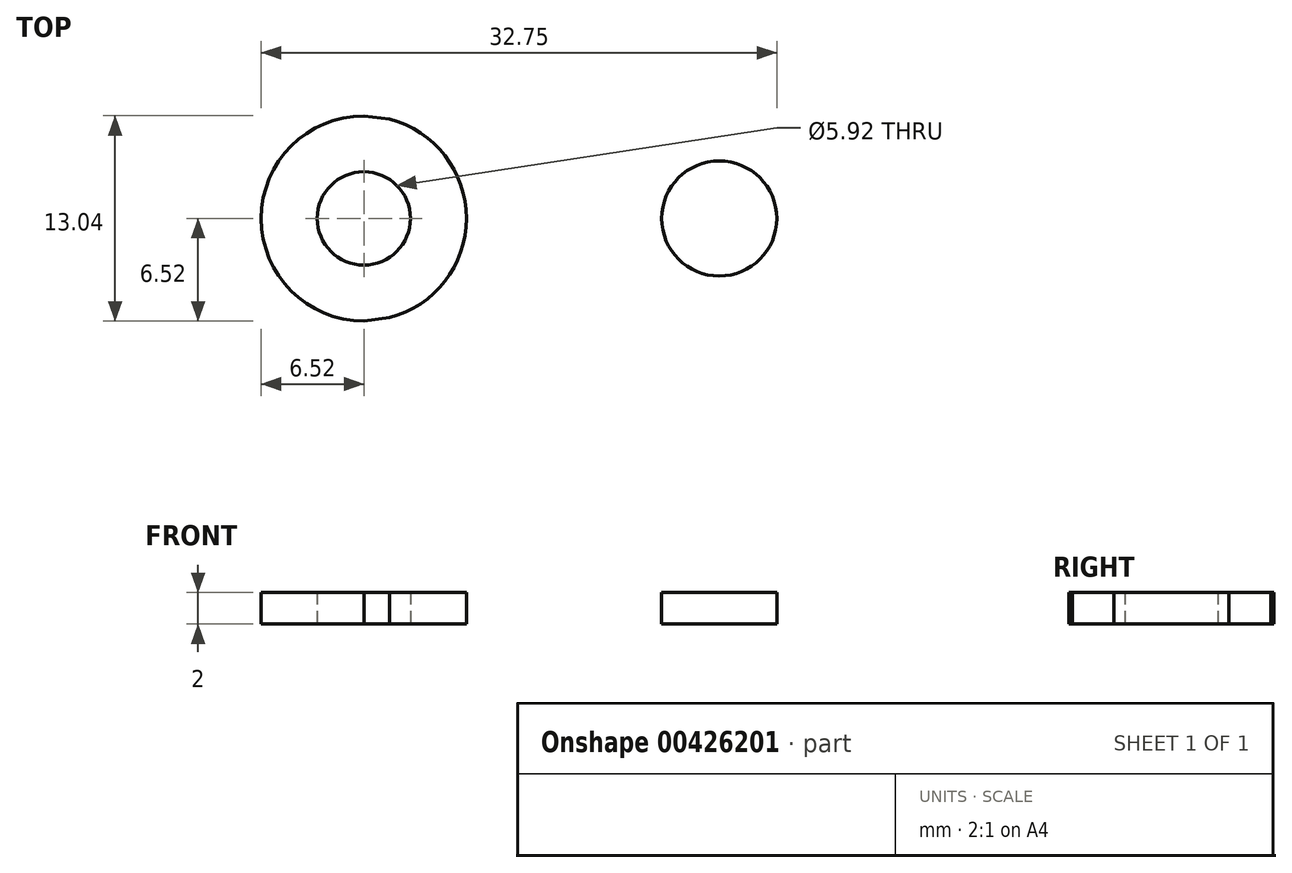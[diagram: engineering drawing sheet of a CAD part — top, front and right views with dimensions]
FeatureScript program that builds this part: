
annotation { "Feature Type Name" : "Feature", "Feature Type Description" : "" }
export const myFeature = defineFeature(function(context is Context, id is Id, definition is map)
    precondition{}
    {
        {
            var Q0;
            Q0=qCreatedBy(makeId("Top.planeOp"),FACE);
            var sketch = newSketch(context, id + "F0", { "sketchPlane" : qUnion([Q0])});
            skCircle(sketch, "E0", {"center": v(0, 0) * mm, "radius": 2.96 * mm});
            skCircle(sketch, "E1", {"center": v(0, 0) * mm, "radius": 6.52 * mm});
            skCircle(sketch, "E2", {"center": v(22.57, 0) * mm, "radius": 3.66 * mm});
            skLineSegment(sketch, "E3", {"start": v(0, 6.52) * mm, "end": v(22.57, 3.66) * mm});
            skLineSegment(sketch, "E4", {"start": v(0, -6.52) * mm, "end": v(22.57, -3.66) * mm});
            skSolve(sketch);
        }
        {
            var Q0;
            Q0=makeQuery(id+"F0.imprint","IMPRINT",FACE,{"disambiguationData":[TD([[makeQuery(id+"F0.imprint","IMPRINT",EDGE,{"derivedFrom":sQuery(id+"F0.wireOp",EDGE,"E0")}),-1.0]])]});
            var Q1;
            {var subQ0=sQuery(id+"F0.wireOp",EDGE,"E2");var subQ1=makeQuery(id+"F0.imprint","INTERSECT",VERTEX,{"derivedFrom":[subQ0,sQuery(id+"F0.wireOp",EDGE,"E3")]});Q1=makeQuery(id+"F0.imprint","IMPRINT",FACE,{"disambiguationData":[TD([[makeQuery(id+"F0.imprint","IMPRINT",EDGE,{"disambiguationData":[TD([[subQ1,-1.0]])],"derivedFrom":subQ0}),1.0]])]});}
            var Q2;
            {var subQ0=sQuery(id+"F0.wireOp",EDGE,"E3");var subQ1=sQuery(id+"F0.wireOp",EDGE,"E1");var subQ2=makeQuery(id+"F0.imprint","INTERSECT",VERTEX,{"disambiguationData":[OD(1.0)],"derivedFrom":[subQ1,subQ0]});Q2=makeQuery(id+"F0.imprint","IMPRINT",FACE,{"disambiguationData":[TD([[makeQuery(id+"F0.imprint","IMPRINT",EDGE,{"disambiguationData":[TD([[subQ2,1.0]])],"derivedFrom":subQ1}),-1.0]])]});}
            var Q3;
            Q3=sQuery(id+"F0.wireOp",EDGE,"E0");
            var Q4;
            Q4=sQuery(id+"F0.wireOp",EDGE,"E1");
            extrude(context, id + "F1", {"entities" : qUnion([Q0, Q1, Q2]), "surfaceEntities" : qUnion([Q3, Q4]), "depth" : 2 * mm});
        }
        {
            var Q0;
            Q0=makeQuery(id+"F1.opExtrude","CAP_FACE",FACE,{"disambiguationData":[OSD([sQuery(id+"F0.wireOp",EDGE,"E0"),sQuery(id+"F0.wireOp",EDGE,"E1"),sQuery(id+"F0.wireOp",EDGE,"E2"),sQuery(id+"F0.wireOp",EDGE,"E3"),sQuery(id+"F0.wireOp",EDGE,"E4")])],"isStart":false});
            var sketch = newSketch(context, id + "F2", { "sketchPlane" : qUnion([Q0])});
            skCircle(sketch, "E5", {"center": v(22.57, 0) * mm, "radius": 0.99 * mm});
            skSolve(sketch);
        }
        {
            var Q0;
            Q0=makeQuery(id+"F2.imprint","IMPRINT",FACE,{"disambiguationData":[TD([[makeQuery(id+"F2.imprint","IMPRINT",EDGE,{"derivedFrom":sQuery(id+"F2.wireOp",EDGE,"E5")}),1.0]])]});
            var Q1;
            Q1=sQuery(id+"F2.wireOp",EDGE,"E5");
            extrude(context, id + "F3", {"entities" : qUnion([Q0]), "operationType" : NewBodyOperationType.REMOVE, "surfaceEntities" : qUnion([Q1]), "depth" : 10 * mm});
        }
    });
